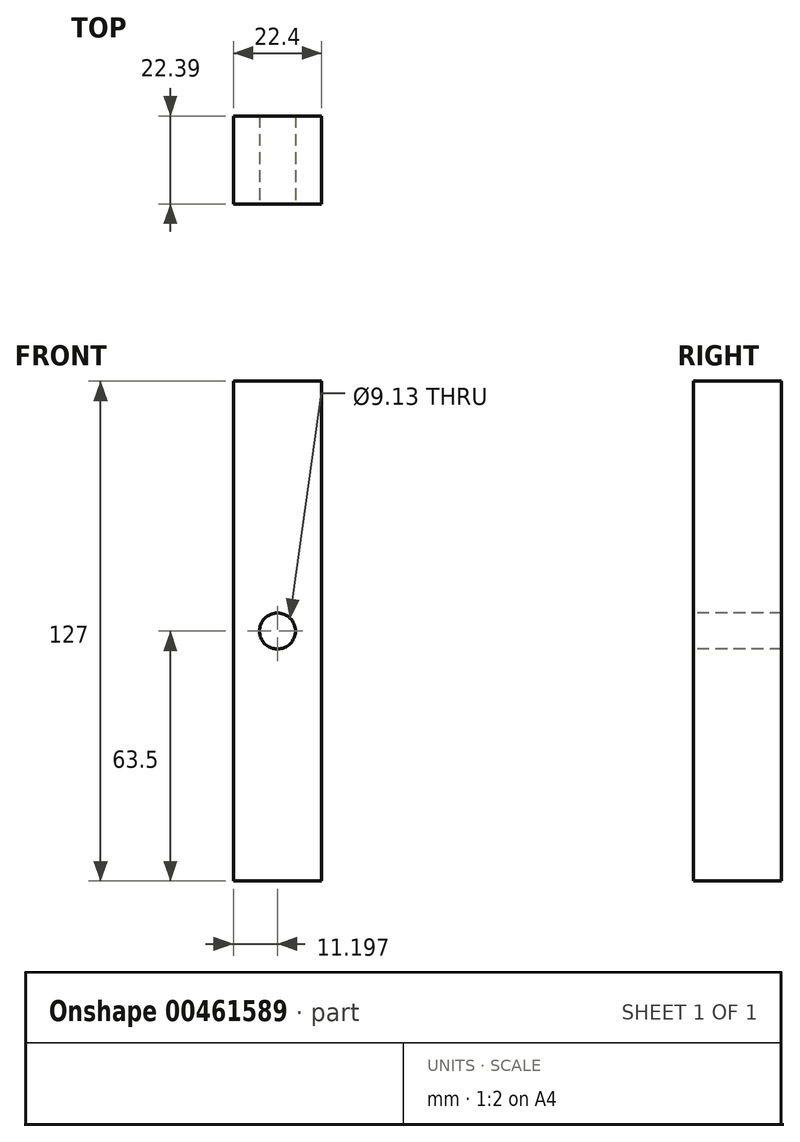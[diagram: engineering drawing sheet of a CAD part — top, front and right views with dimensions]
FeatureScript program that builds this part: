
annotation { "Feature Type Name" : "Feature", "Feature Type Description" : "" }
export const myFeature = defineFeature(function(context is Context, id is Id, definition is map)
    precondition{}
    {
        {
            var Q0;
            Q0=qCreatedBy(makeId("Top.planeOp"),FACE);
            var sketch = newSketch(context, id + "F0", { "sketchPlane" : qUnion([Q0])});
            skLineSegment(sketch, "E0.bottom", {"start": v(-32.14, 64.8) * mm, "end": v(-9.74, 64.8) * mm});
            skLineSegment(sketch, "E0.top", {"start": v(-32.14, 42.4) * mm, "end": v(-9.74, 42.4) * mm});
            skLineSegment(sketch, "E0.left", {"start": v(-32.14, 64.8) * mm, "end": v(-32.14, 42.4) * mm});
            skLineSegment(sketch, "E0.right", {"start": v(-9.74, 64.8) * mm, "end": v(-9.74, 42.4) * mm});
            skSolve(sketch);
        }
        {
            var Q0;
            Q0 = qSketchRegion(id + "F0", true);
            extrude(context, id + "F1", {"entities" : qUnion([Q0]), "oppositeDirection" : true, "depth" : 127 * mm});
        }
        {
            var Q0;
            Q0=makeQuery(id+"F1.opExtrude","SWEPT_FACE",FACE,{"disambiguationData":[OSD([sQuery(id+"F0.wireOp",EDGE,"E0.top")])]});
            var sketch = newSketch(context, id + "F2", { "sketchPlane" : qUnion([Q0])});
            skCircle(sketch, "E1", {"center": v(-20.94, -63.5) * mm, "radius": 4.56 * mm});
            skLineSegment(sketch, "E2", {"start": v(-20.94, 0) * mm, "end": v(-20.94, -127) * mm, "construction": true});
            skSolve(sketch);
        }
        {
            var Q0;
            Q0 = qSketchRegion(id + "F2", true);
            extrude(context, id + "F3", {"entities" : qUnion([Q0]), "operationType" : NewBodyOperationType.REMOVE, "endBound" : BoundingType.THROUGH_ALL, "oppositeDirection" : true, "depth" : 25.4 * mm});
        }
    });
